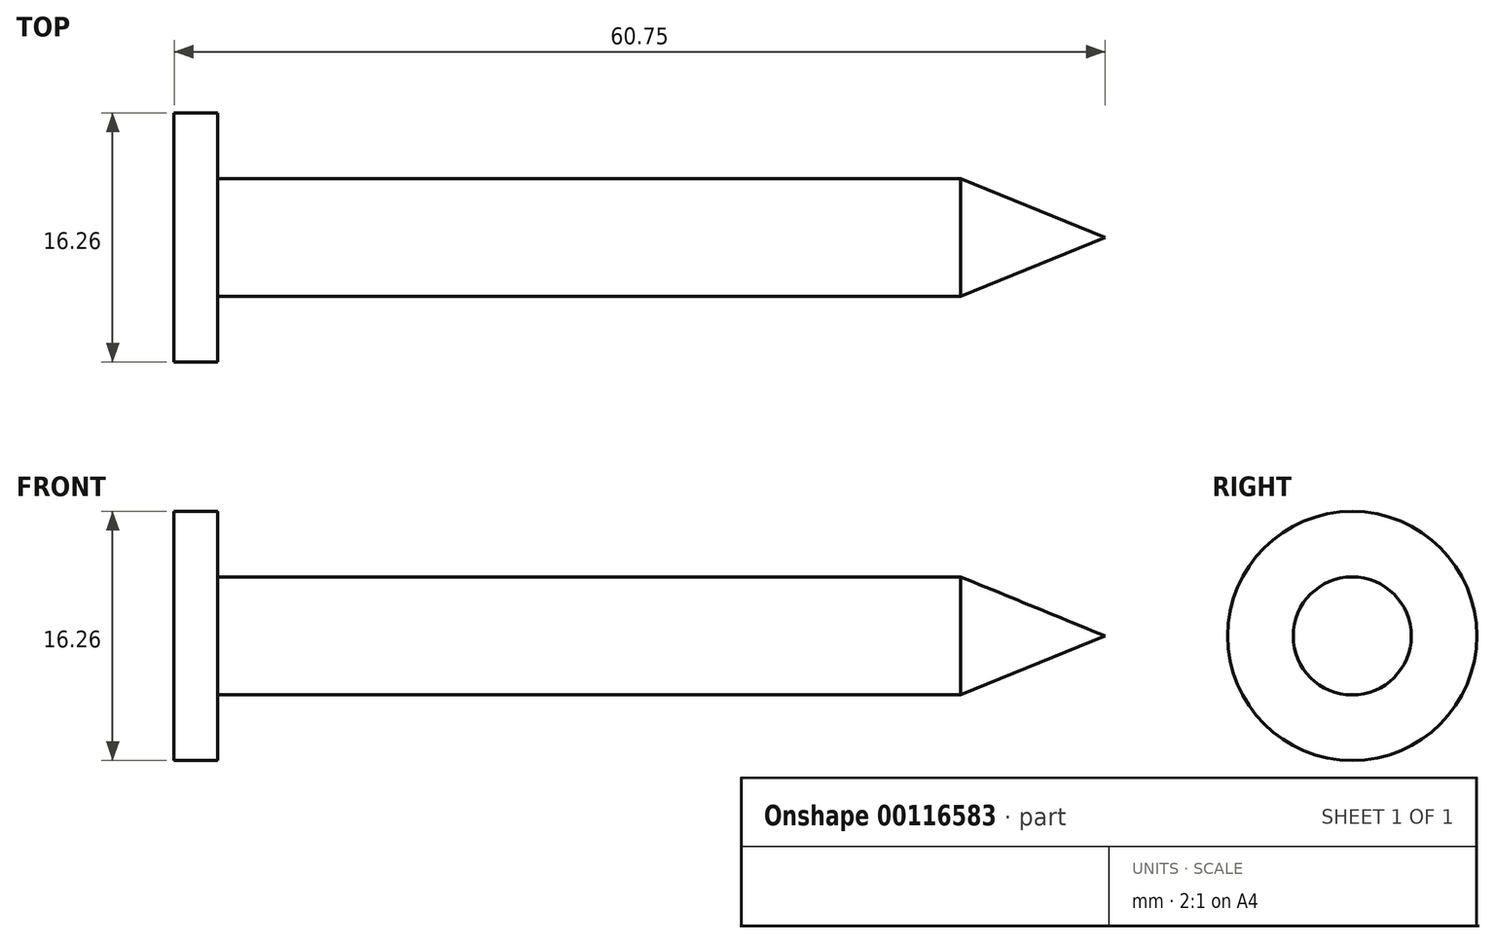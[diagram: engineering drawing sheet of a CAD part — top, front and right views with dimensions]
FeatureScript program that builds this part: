
annotation { "Feature Type Name" : "Feature", "Feature Type Description" : "" }
export const myFeature = defineFeature(function(context is Context, id is Id, definition is map)
    precondition{}
    {
        {
            var Q0;
            Q0=qCreatedBy(makeId("Front.planeOp"),FACE);
            var sketch = newSketch(context, id + "F0", { "sketchPlane" : qUnion([Q0])});
            skLineSegment(sketch, "E0.bottom", {"start": v(-7.7, 0) * mm, "end": v(40.79, 0) * mm});
            skLineSegment(sketch, "E0.top", {"start": v(-7.7, 3.85) * mm, "end": v(40.79, 3.85) * mm});
            skLineSegment(sketch, "E0.left", {"start": v(-7.7, 0) * mm, "end": v(-7.7, 3.85) * mm});
            skLineSegment(sketch, "E0.right", {"start": v(40.79, 0) * mm, "end": v(40.79, 3.85) * mm});
            skLineSegment(sketch, "E1", {"start": v(40.79, 3.85) * mm, "end": v(50.2, 0) * mm});
            skLineSegment(sketch, "E2", {"start": v(50.2, 0) * mm, "end": v(40.79, 0) * mm});
            skLineSegment(sketch, "E3.bottom", {"start": v(-7.7, 0) * mm, "end": v(-10.55, 0) * mm});
            skLineSegment(sketch, "E3.top", {"start": v(-7.7, 8.13) * mm, "end": v(-10.55, 8.13) * mm});
            skLineSegment(sketch, "E3.left", {"start": v(-7.7, 0) * mm, "end": v(-7.7, 8.13) * mm});
            skLineSegment(sketch, "E3.right", {"start": v(-10.55, 0) * mm, "end": v(-10.55, 8.13) * mm});
            skSolve(sketch);
        }
        {
            var Q0;
            {var subQ0=sQuery(id+"F0.wireOp",EDGE,"E0.bottom");Q0=makeQuery(id+"F0.imprint","IMPRINT",FACE,{"disambiguationData":[TD([[makeQuery(id+"F0.imprint","IMPRINT",EDGE,{"derivedFrom":subQ0}),1.0]])]});}
            var Q1;
            Q1=makeQuery(id+"F0.imprint","IMPRINT",FACE,{"disambiguationData":[TD([[makeQuery(id+"F0.imprint","IMPRINT",EDGE,{"derivedFrom":sQuery(id+"F0.wireOp",EDGE,"E0.right")}),-1.0]])]});
            var Q2;
            Q2=sQuery(id+"F0.wireOp",EDGE,"E0.bottom");
            revolve(context, id + "F1", {"entities" : qUnion([Q0, Q1]), "axis" : qUnion([Q2]), "revolveType" : RevolveType.FULL});
        }
        {
            var Q0;
            {var subQ3=sQuery(id+"F0.wireOp",EDGE,"E3.bottom");Q0=makeQuery(id+"F0.imprint","IMPRINT",FACE,{"disambiguationData":[TD([[makeQuery(id+"F0.imprint","IMPRINT",EDGE,{"derivedFrom":subQ3}),-1.0]])]});}
            var Q1;
            Q1=sQuery(id+"F0.wireOp",EDGE,"E3.bottom");
            revolve(context, id + "F2", {"operationType" : NewBodyOperationType.ADD, "entities" : qUnion([Q0]), "axis" : qUnion([Q1]), "revolveType" : RevolveType.FULL});
        }
    });
